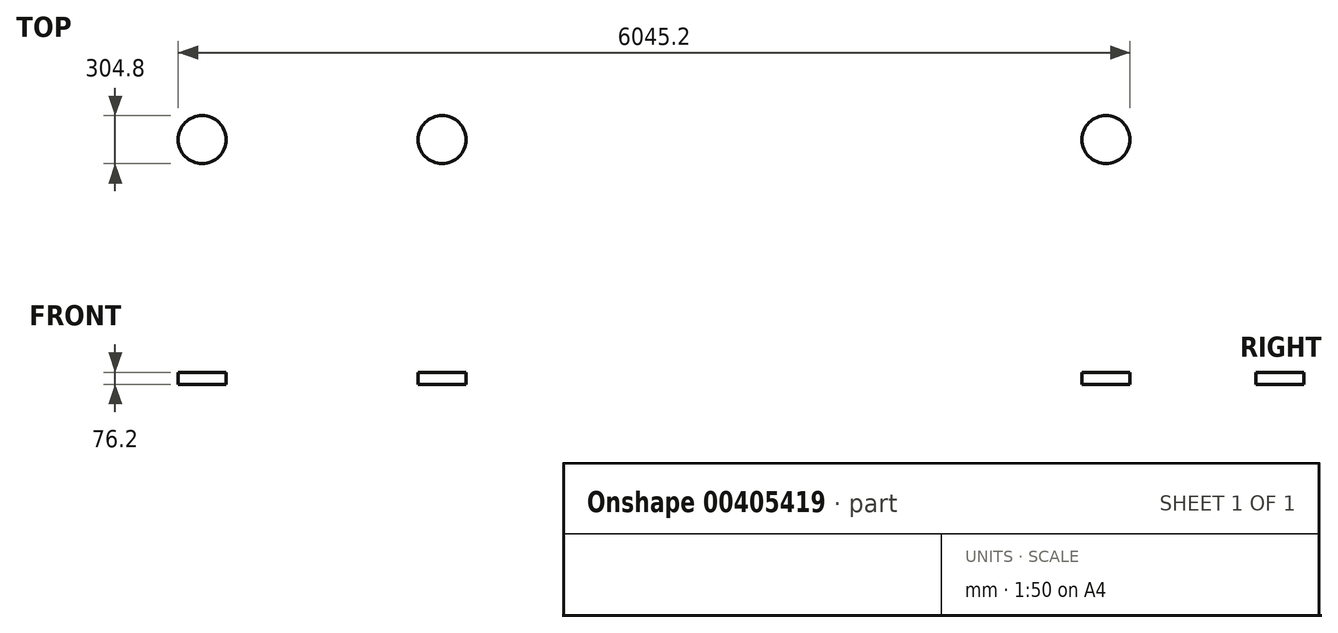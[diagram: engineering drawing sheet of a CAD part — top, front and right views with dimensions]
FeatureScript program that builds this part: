
annotation { "Feature Type Name" : "Feature", "Feature Type Description" : "" }
export const myFeature = defineFeature(function(context is Context, id is Id, definition is map)
    precondition{}
    {
        {
            var Q0;
            Q0=qCreatedBy(makeId("Top.planeOp"),FACE);
            var sketch = newSketch(context, id + "F0", { "sketchPlane" : qUnion([Q0])});
            skLineSegment(sketch, "E0.bottom", {"start": v(-3056.66, 152.4) * mm, "end": v(2988.54, 152.4) * mm});
            skLineSegment(sketch, "E0.top", {"start": v(-3056.66, -152.4) * mm, "end": v(2988.54, -152.4) * mm});
            skLineSegment(sketch, "E0.left", {"start": v(-3056.66, 152.4) * mm, "end": v(-3056.66, -152.4) * mm});
            skLineSegment(sketch, "E0.right", {"start": v(2988.54, 152.4) * mm, "end": v(2988.54, -152.4) * mm});
            skCircle(sketch, "E1", {"center": v(-2904.26, 0) * mm, "radius": 152.4 * mm});
            skCircle(sketch, "E2", {"center": v(-1380.26, 0) * mm, "radius": 152.4 * mm});
            skCircle(sketch, "E3", {"center": v(2836.14, 0) * mm, "radius": 152.4 * mm});
            skSolve(sketch);
        }
        {
            var Q0;
            {var subQ0=sQuery(id+"F0.wireOp",EDGE,"E1");var subQ1=makeQuery(id+"F0.imprint","INTERSECT",VERTEX,{"derivedFrom":[sQuery(id+"F0.wireOp",EDGE,"E0.bottom"),subQ0]});Q0=makeQuery(id+"F0.imprint","IMPRINT",FACE,{"disambiguationData":[TD([[makeQuery(id+"F0.imprint","IMPRINT",EDGE,{"disambiguationData":[TD([[subQ1,-1.0]])],"derivedFrom":subQ0}),1.0]])]});}
            var Q1;
            {var subQ0=sQuery(id+"F0.wireOp",EDGE,"E2");var subQ1=makeQuery(id+"F0.imprint","INTERSECT",VERTEX,{"derivedFrom":[sQuery(id+"F0.wireOp",EDGE,"E0.bottom"),subQ0]});Q1=makeQuery(id+"F0.imprint","IMPRINT",FACE,{"disambiguationData":[TD([[makeQuery(id+"F0.imprint","IMPRINT",EDGE,{"disambiguationData":[TD([[subQ1,-1.0]])],"derivedFrom":subQ0}),1.0]])]});}
            var Q2;
            {var subQ0=sQuery(id+"F0.wireOp",EDGE,"E3");var subQ1=makeQuery(id+"F0.imprint","INTERSECT",VERTEX,{"derivedFrom":[sQuery(id+"F0.wireOp",EDGE,"E0.bottom"),subQ0]});Q2=makeQuery(id+"F0.imprint","IMPRINT",FACE,{"disambiguationData":[TD([[makeQuery(id+"F0.imprint","IMPRINT",EDGE,{"disambiguationData":[TD([[subQ1,1.0]])],"derivedFrom":subQ0}),1.0]])]});}
            extrude(context, id + "F1", {"entities" : qUnion([Q0, Q1, Q2]), "depth" : 76.2 * mm});
        }
    });
